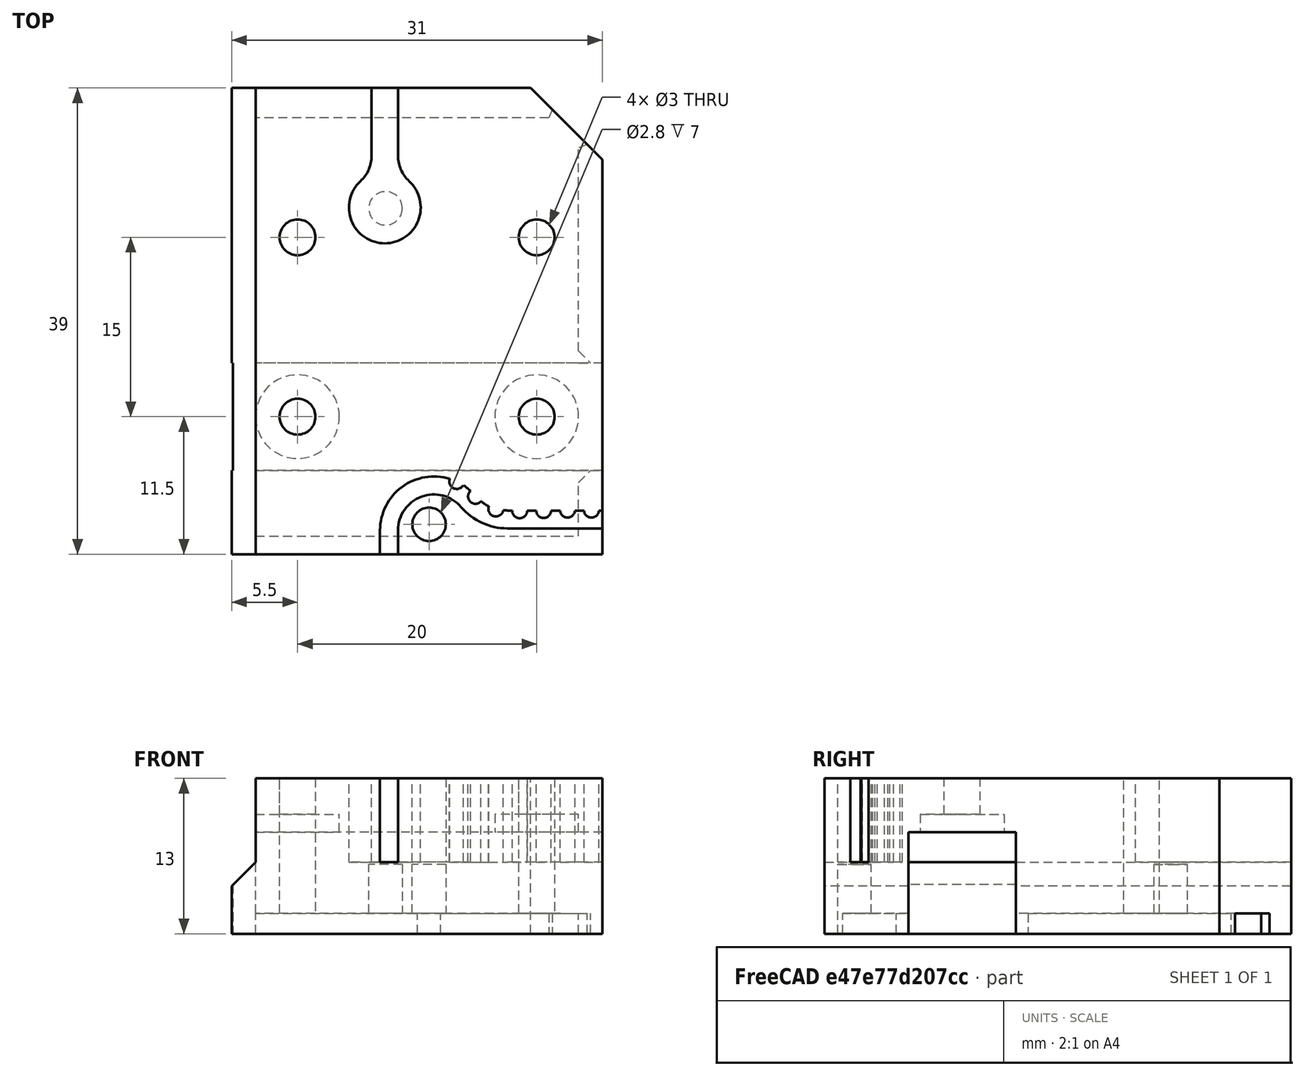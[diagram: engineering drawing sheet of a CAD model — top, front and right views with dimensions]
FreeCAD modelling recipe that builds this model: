
FCSTD DOCUMENT  (FreeCAD 0.19R)
Label: Yjoint_bolted
License: All rights reserved
LicenseURL: http://en.wikipedia.org/wiki/All_rights_reserved
objects: Sketcher::SketchObject×13, PartDesign::Pocket×10, PartDesign::Pad×3, PartDesign::Chamfer×1, PartDesign::Body×1, Mesh::Feature×1
note: 42 computed .brp shape members not serialized (recipe doc carries the construction recipe); baked Part::Feature solids carry a one-line shape summary decoded from their .brp

FEATURE [Sketcher::SketchObject] Sketch
  FullyConstrained = false
  MapMode = 5
  Support = -> [XY_Plane]
  sketch-geometry (9):
    g0: LineSegment StartX=-15.5 StartY=20 StartZ=0 EndX=15.5 EndY=20 EndZ=0
    g1: LineSegment StartX=15.5 StartY=20 StartZ=0 EndX=15.5 EndY=-19 EndZ=0
    g2: LineSegment StartX=15.5 StartY=-19 StartZ=0 EndX=-15.5 EndY=-19 EndZ=0
    g3: LineSegment StartX=-15.5 StartY=-19 StartZ=0 EndX=-15.5 EndY=20 EndZ=0
    g4: LineSegment StartX=-37.8866 StartY=-3 StartZ=0 EndX=43.1927 EndY=-3 EndZ=0
    g5: LineSegment StartX=43.1927 StartY=-3 StartZ=0 EndX=43.1927 EndY=-12 EndZ=0
    g6: LineSegment StartX=43.1927 StartY=-12 StartZ=0 EndX=-37.8866 EndY=-12 EndZ=0
    g7: LineSegment StartX=-37.8866 StartY=-12 StartZ=0 EndX=-37.8866 EndY=-3 EndZ=0
    g8: LineSegment StartX=-54.8094 StartY=-7.5 StartZ=0 EndX=51.9088 EndY=-7.5 EndZ=0
  constraints (22):
    c: Coincident(g0,g1)
    c: Coincident(g1,g2)
    c: Coincident(g2,g3)
    c: Coincident(g3,g0)
    c: Horizontal(g2)
    c: Vertical(g1)
    c: Vertical(g3)
    c: Distance(g2) = 31
    c: Coincident(g4,g5)
    c: Coincident(g5,g6)
    c: Coincident(g6,g7)
    c: Coincident(g7,g4)
    c: Horizontal(g4)
    c: Horizontal(g6)
    c: Vertical(g5)
    c: Vertical(g7)
    c: Symmetric(g5,g4,g8)
    c: DistanceY(g8) = -7.5
    c: Distance(g5) = 9
    c: Distance(g0,g4) = 23
    c: Symmetric(g0,g0,g-2)
    c: DistanceY(g1) = -19
FEATURE [PartDesign::Pad] Pad
  Direction = (1,1,1)
  Length = 13
  Length2 = 100
  Profile = -> Sketch
  Type = 0
FEATURE [Sketcher::SketchObject] Sketch001  label="beltreleif"
  FullyConstrained = false
  MapMode = 5
  Placement = pos=(0,-19,0) rot=(1,0,0;1.5708rad)
  Support = -> [Pad]
  sketch-geometry (3):
    g0: LineSegment StartX=-23.4183 StartY=-3.91832 StartZ=0 EndX=-13.5 EndY=6 EndZ=0
    g1: LineSegment StartX=-13.5 StartY=6 StartZ=0 EndX=-13.5 EndY=30.99 EndZ=0
    g2: LineSegment StartX=-13.5 StartY=30.99 StartZ=0 EndX=-23.4183 EndY=-3.91832 EndZ=0
  constraints (8):
    c: Coincident(g0,g1)
    c: Vertical(g1)
    c: Coincident(g1,g2)
    c: Coincident(g2,g0)
    c: Angle(g0) = 0.785398
    c: DistanceX(g0) = -13.5
    c: Distance(g2) = 36.29
    c: DistanceY(g0) = 6
FEATURE [PartDesign::Pocket] Pocket
  BaseFeature = -> Pad
  Length = 5
  Length2 = 100
  Profile = -> Sketch001
  Type = 1
FEATURE [Sketcher::SketchObject] Sketch002  label="RailPocket"
  FullyConstrained = false
  MapMode = 5
  Placement = pos=(15.5,0,0) rot=(0.57735,0.57735,0.57735;2.0944rad)
  Support = -> [Pocket]
  sketch-geometry (5):
    g0: LineSegment StartX=-12 StartY=8.5 StartZ=0 EndX=-3 EndY=8.5 EndZ=0
    g1: LineSegment StartX=-3 StartY=8.5 StartZ=0 EndX=-3 EndY=-7.81784 EndZ=0
    g2: LineSegment StartX=-3 StartY=-7.81784 StartZ=0 EndX=-12 EndY=-7.81784 EndZ=0
    g3: LineSegment StartX=-12 StartY=-7.81784 StartZ=0 EndX=-12 EndY=8.5 EndZ=0
    g4: LineSegment StartX=-7.5 StartY=9.53875 StartZ=0 EndX=-7.5 EndY=-20.3605 EndZ=0
  constraints (12):
    c: Coincident(g0,g1)
    c: Coincident(g1,g2)
    c: Coincident(g2,g3)
    c: Coincident(g3,g0)
    c: Horizontal(g0)
    c: Horizontal(g2)
    c: Vertical(g1)
    c: Vertical(g3)
    c: Distance(g0) = 9
    c: Symmetric(g0,g0,g4)
    c: DistanceX(g4) = -7.5
    c: DistanceY(g0) = 8.5
FEATURE [PartDesign::Pocket] Pocket001
  BaseFeature = -> Pocket
  Length = 29
  Length2 = 100
  Profile = -> Sketch002
  Type = 0
FEATURE [Sketcher::SketchObject] Sketch003  label="CarriageBolts"
  FullyConstrained = true
  MapMode = 5
  Placement = pos=(0,0,13) rot=(0,0,1;0rad)
  Support = -> [Pocket001]
  sketch-geometry (4):
    g0: Circle CenterX=10 CenterY=7.5 CenterZ=0 NormalX=0 NormalY=0 NormalZ=1 AngleXU=0 Radius=1.5
    g1: Circle CenterX=-10 CenterY=7.5 CenterZ=0 NormalX=0 NormalY=0 NormalZ=1 AngleXU=0 Radius=1.5
    g2: Circle CenterX=-10 CenterY=-7.5 CenterZ=0 NormalX=0 NormalY=0 NormalZ=1 AngleXU=0 Radius=1.5
    g3: Circle CenterX=10 CenterY=-7.5 CenterZ=0 NormalX=0 NormalY=0 NormalZ=1 AngleXU=0 Radius=1.5
  constraints (9):
    c: DistanceY(g0) = 7.5
    c: DistanceX(g0) = 10
    c: Symmetric(g1,g0,g-2)
    c: Symmetric(g0,g2,g-1)
    c: Symmetric(g1,g3,g-1)
    c: Diameter(g0) = 3
    c: Equal(g0,g1)
    c: Equal(g0,g2)
    c: Equal(g0,g3)
FEATURE [PartDesign::Pocket] Pocket002
  BaseFeature = -> Pocket001
  Length = 5
  Length2 = 100
  Profile = -> Sketch003
  Type = 1
FEATURE [Sketcher::SketchObject] Sketch004  label="MotorSideBeltClamp"
  FullyConstrained = false
  MapMode = 5
  Placement = pos=(0,0,13) rot=(0,0,1;0rad)
  Support = -> [Pocket002]
  sketch-geometry (13):
    g0: LineSegment StartX=-3.8 StartY=-19.337 StartZ=0 EndX=-3.8 EndY=-36 EndZ=0
    g1: LineSegment StartX=-3.8 StartY=-36 StartZ=0 EndX=-1.6 EndY=-36 EndZ=0
    g2: LineSegment StartX=-1.6 StartY=-36 StartZ=0 EndX=-1.6 EndY=-19.337 EndZ=0
    g3: ArcOfCircle CenterX=-2.7 CenterY=-15 CenterZ=0 NormalX=0 NormalY=0 NormalZ=1 AngleXU=0 Radius=3 StartAngle=5.45738 EndAngle=10.2506
    g4: ArcOfCircle CenterX=1.3 CenterY=-19.337 CenterZ=0 NormalX=0 NormalY=0 NormalZ=1 AngleXU=0 Radius=2.9 StartAngle=2.31579 EndAngle=3.14159
    g5: ArcOfCircle CenterX=-6.7 CenterY=-19.337 CenterZ=0 NormalX=0 NormalY=0 NormalZ=1 AngleXU=0 Radius=2.9 StartAngle=6e-16 EndAngle=0.825804
    g6: LineSegment StartX=-2.7 StartY=-15 StartZ=0 EndX=-2.7 EndY=-40.8271 EndZ=0
    g7: LineSegment StartX=-3.8 StartY=23.44 StartZ=0 EndX=-1.6 EndY=23.44 EndZ=0
    g8: LineSegment StartX=-1.6 StartY=23.44 StartZ=0 EndX=-1.6 EndY=14.337 EndZ=0
    g9: LineSegment StartX=-3.8 StartY=23.44 StartZ=0 EndX=-3.8 EndY=14.337 EndZ=0
    g10: ArcOfCircle CenterX=-2.7 CenterY=10 CenterZ=0 NormalX=0 NormalY=0 NormalZ=1 AngleXU=0 Radius=3 StartAngle=2.31579 EndAngle=7.10899
    g11: ArcOfCircle CenterX=1.3 CenterY=14.337 CenterZ=0 NormalX=0 NormalY=0 NormalZ=1 AngleXU=0 Radius=2.9 StartAngle=3.14159 EndAngle=3.9674
    g12: ArcOfCircle CenterX=-6.7 CenterY=14.337 CenterZ=0 NormalX=0 NormalY=0 NormalZ=1 AngleXU=0 Radius=2.9 StartAngle=5.45738 EndAngle=6.28319
  constraints (32):
    c: Vertical(g0)
    c: Coincident(g0,g1)
    c: Horizontal(g1)
    c: Coincident(g1,g2)
    c: Tangent(g4,g3) = 1.5708
    c: Tangent(g4,g2) = 1.5708
    c: Tangent(g5,g3) = 1.5708
    c: Tangent(g5,g0) = 1.5708
    c: Coincident(g6,g3)
    c: Symmetric(g1,g0,g6)
    c: Symmetric(g2,g0,g6)
    c: DistanceX(g3) = -2.7
    c: Diameter(g3) = 6
    c: Distance(g4,g5) = 8
    c: Distance(g1) = 2.2
    c: DistanceY(g3) = -15
    c: DistanceY(g1) = -36
    c: Coincident(g7,g8)
    c: Vertical(g8)
    c: Coincident(g7,g9)
    c: Tangent(g11,g10) = 1.5708
    c: Diameter(g10) = 6
    c: Tangent(g11,g8) = -1.5708
    c: Tangent(g12,g10) = 1.5708
    c: Tangent(g12,g9) = 1.5708
    c: Symmetric(g7,g7,g6)
    c: Distance(g7) = 2.2
    c: PointOnObject(g10,g6)
    c: Symmetric(g8,g9,g6)
    c: Distance(g11,g12) = 8
    c: DistanceY(g10) = 10
    c: DistanceY(g7) = 23.44
FEATURE [PartDesign::Pocket] Pocket003
  BaseFeature = -> Pocket002
  Length = 7
  Length2 = 100
  Profile = -> Sketch004
  Type = 0
FEATURE [Sketcher::SketchObject] Sketch005  label="BottomPocket"
  FullyConstrained = true
  MapMode = 5
  Placement = pos=(0,0,0) rot=(1,0,0;3.14159rad)
  Support = -> [Pocket003]
  sketch-geometry (4):
    g0: LineSegment StartX=-13.5 StartY=17.5 StartZ=0 EndX=13.5 EndY=17.5 EndZ=0
    g1: LineSegment StartX=13.5 StartY=17.5 StartZ=0 EndX=13.5 EndY=-17.5 EndZ=0
    g2: LineSegment StartX=13.5 StartY=-17.5 StartZ=0 EndX=-13.5 EndY=-17.5 EndZ=0
    g3: LineSegment StartX=-13.5 StartY=-17.5 StartZ=0 EndX=-13.5 EndY=17.5 EndZ=0
  constraints (11):
    c: Coincident(g0,g1)
    c: Coincident(g1,g2)
    c: Coincident(g2,g3)
    c: Coincident(g3,g0)
    c: Horizontal(g2)
    c: Vertical(g1)
    c: Vertical(g3)
    c: Distance(g0) = 27
    c: Distance(g1) = 35
    c: Symmetric(g0,g2,g-1)
    c: Horizontal(g0)
FEATURE [PartDesign::Pocket] Pocket004
  BaseFeature = -> Pocket003
  Length = 1.7
  Length2 = 100
  Profile = -> Sketch005
  Type = 0
FEATURE [Sketcher::SketchObject] Sketch006  label="CornerClip"
  FullyConstrained = false
  MapMode = 5
  Placement = pos=(0,0,13) rot=(0,0,1;0rad)
  Support = -> [Pocket004]
  sketch-geometry (3):
    g0: LineSegment StartX=1.95516 StartY=27.5448 StartZ=0 EndX=15.5 EndY=14 EndZ=0
    g1: LineSegment StartX=15.5 StartY=14 StartZ=0 EndX=15.5 EndY=27.5448 EndZ=0
    g2: LineSegment StartX=15.5 StartY=27.5448 StartZ=0 EndX=1.95516 EndY=27.5448 EndZ=0
  constraints (8):
    c: Coincident(g0,g1)
    c: Vertical(g1)
    c: Coincident(g1,g2)
    c: Horizontal(g2)
    c: Coincident(g0,g2)
    c: Angle(g0) = -0.785398
    c: DistanceX(g0) = 15.5
    c: DistanceY(g0) = 14
FEATURE [PartDesign::Pocket] Pocket005
  BaseFeature = -> Pocket004
  Length = 5
  Length2 = 100
  Profile = -> Sketch006
  Type = 1
FEATURE [Sketcher::SketchObject] Sketch007  label="clampHole"
  ExternalGeometry = -> [Pocket005]
  FullyConstrained = false
  MapMode = 5
  Placement = pos=(0,0,13) rot=(0,0,1;0rad)
  Support = -> [Pocket005]
  sketch-geometry (2):
    g0: Circle CenterX=-2.63724 CenterY=9.92805 CenterZ=0 NormalX=0 NormalY=0 NormalZ=1 AngleXU=0 Radius=1.4
    g1: Circle CenterX=1 CenterY=-16.5 CenterZ=0 NormalX=0 NormalY=0 NormalZ=1 AngleXU=0 Radius=1.4
  constraints (4):
    c: Diameter(g0) = 2.8
    c: Diameter(g1) = 2.8
    c: DistanceY(g1) = -16.5
    c: DistanceX(g1) = 1
FEATURE [Sketcher::SketchObject] Sketch008  label="printFilm"
  FullyConstrained = false
  MapMode = 5
  Placement = pos=(0,0,6) rot=(0,0,1;0rad)
  sketch-geometry (8):
    g0: LineSegment StartX=-7.42355 StartY=14.214 StartZ=0 EndX=2.97442 EndY=14.214 EndZ=0
    g1: LineSegment StartX=2.97442 StartY=14.214 StartZ=0 EndX=2.97442 EndY=6.02841 EndZ=0
    g2: LineSegment StartX=2.97442 StartY=6.02841 StartZ=0 EndX=-7.42355 EndY=6.02841 EndZ=0
    g3: LineSegment StartX=-7.42355 StartY=6.02841 StartZ=0 EndX=-7.42355 EndY=14.214 EndZ=0
    g4: LineSegment StartX=-5.71547 StartY=-12.14 StartZ=0 EndX=6.63722 EndY=-12.14 EndZ=0
    g5: LineSegment StartX=6.63722 StartY=-12.14 StartZ=0 EndX=6.63722 EndY=-18.9745 EndZ=0
    g6: LineSegment StartX=6.63722 StartY=-18.9745 StartZ=0 EndX=-5.71547 EndY=-18.9745 EndZ=0
    g7: LineSegment StartX=-5.71547 StartY=-18.9745 StartZ=0 EndX=-5.71547 EndY=-12.14 EndZ=0
  constraints (16):
    c: Coincident(g0,g1)
    c: Coincident(g1,g2)
    c: Coincident(g2,g3)
    c: Coincident(g3,g0)
    c: Horizontal(g0)
    c: Horizontal(g2)
    c: Vertical(g1)
    c: Vertical(g3)
    c: Coincident(g4,g5)
    c: Coincident(g5,g6)
    c: Coincident(g6,g7)
    c: Coincident(g7,g4)
    c: Horizontal(g4)
    c: Horizontal(g6)
    c: Vertical(g5)
    c: Vertical(g7)
FEATURE [Sketcher::SketchObject] Sketch009  label="BeltTrap1"
  FullyConstrained = true
  MapMode = 5
  Placement = pos=(0,0,13) rot=(0,0,1;0rad)
  sketch-geometry (12):
    g0: ArcOfCircle CenterX=1.4 CenterY=-17 CenterZ=0 NormalX=0 NormalY=0 NormalZ=1 AngleXU=0 Radius=3 StartAngle=0.70304 EndAngle=3.14159
    g1: ArcOfCircle CenterX=1.4 CenterY=-17 CenterZ=0 NormalX=0 NormalY=0 NormalZ=1 AngleXU=0 Radius=4.5 StartAngle=0.70304 EndAngle=3.14159
    g2: LineSegment StartX=-3.1 StartY=-17 StartZ=0 EndX=-1.6 EndY=-17 EndZ=0
    g3: LineSegment StartX=-1.6 StartY=-17 StartZ=0 EndX=-1.6 EndY=-20.87 EndZ=0
    g4: LineSegment StartX=-1.6 StartY=-20.87 StartZ=0 EndX=-3.1 EndY=-20.87 EndZ=0
    g5: LineSegment StartX=-3.1 StartY=-20.87 StartZ=0 EndX=-3.1 EndY=-17 EndZ=0
    g6: LineSegment StartX=-4.78 StartY=-17 StartZ=0 EndX=6 EndY=-17 EndZ=0
    g7: ArcOfCircle CenterX=7.5411 CenterY=-11.7954 CenterZ=0 NormalX=0 NormalY=0 NormalZ=1 AngleXU=0 Radius=3.54989 StartAngle=3.84463 EndAngle=4.71239
    g8: ArcOfCircle CenterX=7.5411 CenterY=-11.7954 CenterZ=0 NormalX=0 NormalY=0 NormalZ=1 AngleXU=0 Radius=5.04989 StartAngle=3.84463 EndAngle=4.71239
    g9: LineSegment StartX=21.71 StartY=-15.3453 StartZ=0 EndX=7.5411 EndY=-15.3453 EndZ=0
    g10: LineSegment StartX=21.71 StartY=-16.8453 StartZ=0 EndX=7.5411 EndY=-16.8453 EndZ=0
    g11: LineSegment StartX=21.71 StartY=-15.3453 StartZ=0 EndX=21.71 EndY=-16.8453 EndZ=0
  constraints (34):
    c: Coincident(g1,g0)
    c: Distance(g0,g0) = 3
    c: DistanceX(g0) = 1.4
    c: Coincident(g2,g1)
    c: Coincident(g2,g0)
    c: Tangent(g0,g3) = -1.5708
    c: Coincident(g3,g4)
    c: Horizontal(g4)
    c: Coincident(g4,g5)
    c: Coincident(g5,g1)
    c: Vertical(g5)
    c: Distance(g4) = 1.5
    c: Distance(g3) = 3.87
    c: Horizontal(g6)
    c: PointOnObject(g0,g6)
    c: PointOnObject(g1,g6)
    c: Parallel(g3,g5)
    c: DistanceY(g6) = -17
    c: Distance(g6) = 10.78
    c: DistanceX(g6) = -4.78
    c: Coincident(g8,g7)
    c: Tangent(g7,g1) = 1.5708
    c: Tangent(g8,g0) = 1.5708
    c: Tangent(g7,g9) = 1.5708
    c: Coincident(g7,g9)
    c: Tangent(g8,g10) = 1.5708
    c: Parallel(g10,g9)
    c: Horizontal(g9)
    c: Coincident(g11,g9)
    c: Coincident(g11,g10)
    c: Vertical(g11)
    c: DistanceX(g9) = 21.71
    c: DistanceX(g8) = 7.5411
    c: DistanceY(g8) = -16.8453
FEATURE [Sketcher::SketchObject] Sketch010
  FullyConstrained = false
  MapMode = 5
  Placement = pos=(0,0,13) rot=(0,0,1;0rad)
  sketch-geometry (7):
    g0: Circle CenterX=3.32107 CenterY=-12.918 CenterZ=0 NormalX=0 NormalY=0 NormalZ=1 AngleXU=0 Radius=0.625
    g1: Circle CenterX=4.888 CenterY=-14.1609 CenterZ=0 NormalX=0 NormalY=0 NormalZ=1 AngleXU=0 Radius=0.625
    g2: Circle CenterX=6.58573 CenterY=-15.2181 CenterZ=0 NormalX=0 NormalY=0 NormalZ=1 AngleXU=0 Radius=0.625
    g3: Circle CenterX=8.58033 CenterY=-15.3649 CenterZ=0 NormalX=0 NormalY=0 NormalZ=1 AngleXU=0 Radius=0.625
    g4: Circle CenterX=10.5802 CenterY=-15.3436 CenterZ=0 NormalX=0 NormalY=0 NormalZ=1 AngleXU=0 Radius=0.625
    g5: Circle CenterX=12.58 CenterY=-15.3146 CenterZ=0 NormalX=0 NormalY=0 NormalZ=1 AngleXU=0 Radius=0.625
    g6: Circle CenterX=14.58 CenterY=-15.3184 CenterZ=0 NormalX=0 NormalY=0 NormalZ=1 AngleXU=0 Radius=0.625
  constraints (10):
    c: Distance(g0,g1) = 2
    c: Distance(g1,g2) = 2
    c: Distance(g2,g3) = 2
    c: Distance(g4,g5) = 2
    c: Distance(g4,g3) = 2
    c: Distance(g6,g5) = 2
    c: DistanceX(g6) = 14.58
    c: Diameter(g6) = 1.25
    c: Diameter(g0) = 1.25
    c: Equal(g0, g1-g5) x5
FEATURE [PartDesign::Pocket] Pocket006
  BaseFeature = -> Pocket005
  Length = 5
  Length2 = 100
  Profile = -> Sketch007
  Type = 1
FEATURE [PartDesign::Pad] Pad001
  BaseFeature = -> Pocket006
  Direction = (1,1,1)
  Length = 0.2
  Length2 = 100
  Profile = -> Sketch008
  Reversed = true
  Type = 0
FEATURE [PartDesign::Pocket] Pocket007
  BaseFeature = -> Pad001
  Length = 7
  Length2 = 100
  Profile = -> Sketch009
  Type = 0
FEATURE [PartDesign::Pad] Pad002
  BaseFeature = -> Pocket007
  Direction = (1,1,1)
  Length = 8
  Length2 = 100
  Profile = -> Sketch010
  Reversed = true
  Type = 0
FEATURE [Sketcher::SketchObject] Sketch011
  FullyConstrained = false
  MapMode = 5
  Placement = pos=(-15.5,0,0) rot=(0.57735,-0.57735,-0.57735;2.0944rad)
  Support = -> [Pad002]
  sketch-geometry (4):
    g0: LineSegment StartX=3 StartY=8.5 StartZ=0 EndX=12 EndY=8.5 EndZ=0
    g1: LineSegment StartX=12 StartY=8.5 StartZ=0 EndX=12 EndY=-1.2366 EndZ=0
    g2: LineSegment StartX=12 StartY=-1.2366 StartZ=0 EndX=3 EndY=-1.2366 EndZ=0
    g3: LineSegment StartX=3 StartY=-1.2366 StartZ=0 EndX=3 EndY=8.5 EndZ=0
  constraints (11):
    c: Coincident(g0,g1)
    c: Coincident(g1,g2)
    c: Coincident(g2,g3)
    c: Coincident(g3,g0)
    c: Horizontal(g0)
    c: Horizontal(g2)
    c: Vertical(g1)
    c: Vertical(g3)
    c: DistanceX(g0) = 3
    c: DistanceX(g0) = 12
    c: DistanceY(g0) = 8.5
FEATURE [PartDesign::Pocket] Pocket008
  BaseFeature = -> Pad002
  Length = 0.1
  Length2 = 100
  Profile = -> Sketch011
  Type = 0
FEATURE [Sketcher::SketchObject] Sketch012
  FullyConstrained = true
  MapMode = 5
  Placement = pos=(0,0,8.5) rot=(1,0,0;3.14159rad)
  sketch-geometry (2):
    g0: Circle CenterX=10 CenterY=7.5 CenterZ=0 NormalX=0 NormalY=0 NormalZ=1 AngleXU=0 Radius=3.5
    g1: Circle CenterX=-10 CenterY=7.5 CenterZ=0 NormalX=0 NormalY=0 NormalZ=1 AngleXU=0 Radius=3.5
  constraints (6):
    c: Diameter(g0) = 7
    c: Equal(g0,g1)
    c: DistanceY(g1) = 7.5
    c: DistanceY(g0) = 7.5
    c: DistanceX(g1) = -10
    c: DistanceX(g0) = 10
FEATURE [PartDesign::Pocket] Pocket009
  BaseFeature = -> Pocket008
  Length = 1.5
  Length2 = 100
  Profile = -> Sketch012
  Type = 0
FEATURE [PartDesign::Chamfer] Chamfer
  Angle = 45
  Base = -> Pocket009 [Edge33,Edge31,Edge92,Edge134]
  BaseFeature = -> Pocket009
  ChamferType = 0
  FlipDirection = false
  Size = 1
  Size2 = 1
  SupportTransform = false
FEATURE [PartDesign::Body] Body
  Group = -> [Sketch,Pad,Sketch001,Pocket,Sketch002,Pocket001,Sketch003,Pocket002,Sketch004,Pocket003,Sketch005,Pocket004,Sketch006,Pocket005,Sketch007,Sketch008,Sketch009,Sketch010,Pocket006,Pad001,Pocket007,Pad002,Sketch011,Pocket008,Sketch012,Pocket009,Chamfer]
  Origin = -> Origin
  Tip = -> Chamfer
FEATURE [Mesh::Feature] Mesh  label="Chamfer (Meshed)"
